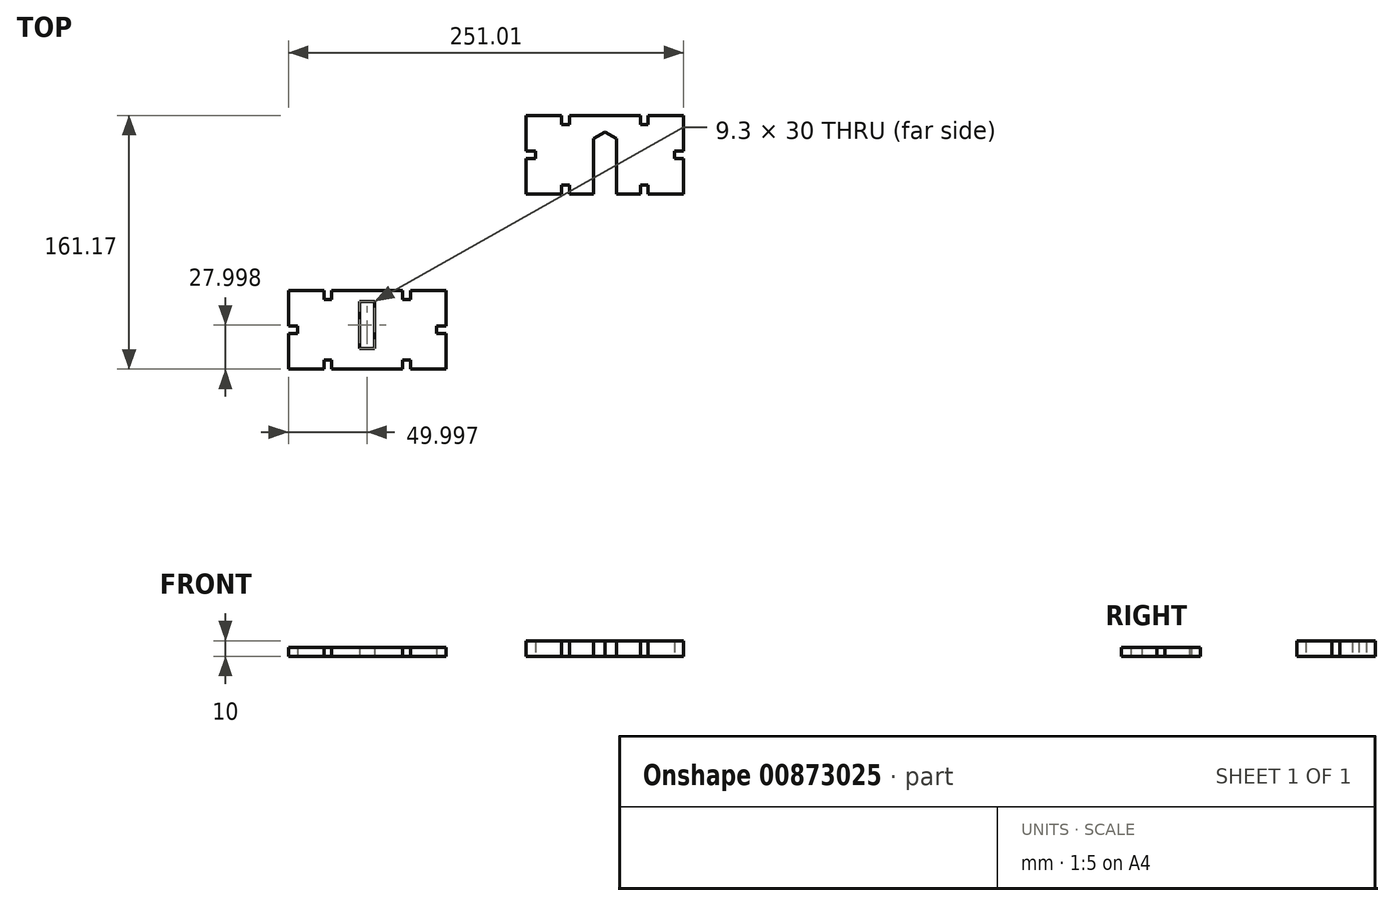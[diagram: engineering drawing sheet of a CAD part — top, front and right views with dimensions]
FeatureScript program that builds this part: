
annotation { "Feature Type Name" : "Feature", "Feature Type Description" : "" }
export const myFeature = defineFeature(function(context is Context, id is Id, definition is map)
    precondition{}
    {
        {
            assignVariable(context, id + "F0", {"name" : "poly_thick", "anyValue" : 5.8});
        }
        {
            var Q0;
            Q0=qCreatedBy(makeId("Top.planeOp"),FACE);
            var sketch = newSketch(context, id + "F1", { "sketchPlane" : qUnion([Q0])});
            skLineSegment(sketch, "E0.bottom", {"start": v(0, 0) * mm, "end": v(22.5, 0) * mm});
            skLineSegment(sketch, "E0.top", {"start": v(0, 50) * mm, "end": v(22.5, 50) * mm});
            skLineSegment(sketch, "E0.left", {"start": v(0, 0) * mm, "end": v(0, 22.5) * mm});
            skLineSegment(sketch, "E0.right", {"start": v(100, 0) * mm, "end": v(100, 22.5) * mm});
            skLineSegment(sketch, "E1.left", {"start": v(42.75, 0) * mm, "end": v(42.75, 35.4) * mm});
            skLineSegment(sketch, "E1.right", {"start": v(57.25, 0) * mm, "end": v(57.25, 35.4) * mm});
            skLineSegment(sketch, "E2", {"start": v(57.25, 35.4) * mm, "end": v(100, 35.4) * mm, "construction": true});
            skLineSegment(sketch, "E3", {"start": v(42.75, 35.4) * mm, "end": v(0, 35.4) * mm, "construction": true});
            skLineSegment(sketch, "E4", {"start": v(50, 0) * mm, "end": v(50, 50) * mm, "construction": true});
            skLineSegment(sketch, "E5", {"start": v(42.75, 35.4) * mm, "end": v(50, 39.58) * mm});
            skLineSegment(sketch, "E6", {"start": v(50, 39.58) * mm, "end": v(57.25, 35.4) * mm});
            skLineSegment(sketch, "E7.trimOffspring", {"start": v(57.25, 0) * mm, "end": v(72.5, 0) * mm});
            skLineSegment(sketch, "E8.bottom", {"start": v(100, 22.5) * mm, "end": v(94.2, 22.5) * mm});
            skLineSegment(sketch, "E8.top", {"start": v(100, 27.5) * mm, "end": v(94.2, 27.5) * mm});
            skLineSegment(sketch, "E8.right", {"start": v(94.2, 22.5) * mm, "end": v(94.2, 27.5) * mm});
            skLineSegment(sketch, "E9", {"start": v(94.2, 22.5) * mm, "end": v(94.2, 0) * mm, "construction": true});
            skLineSegment(sketch, "E10", {"start": v(94.2, 27.5) * mm, "end": v(94.2, 50) * mm, "construction": true});
            skLineSegment(sketch, "E11.MirrorCS", {"start": v(0, 22.5) * mm, "end": v(5.8, 22.5) * mm});
            skLineSegment(sketch, "E12.MirrorCS", {"start": v(5.8, 22.5) * mm, "end": v(5.8, 27.5) * mm});
            skLineSegment(sketch, "E13.MirrorCS", {"start": v(0, 27.5) * mm, "end": v(5.8, 27.5) * mm});
            skLineSegment(sketch, "E14.trimOffspring", {"start": v(0, 27.5) * mm, "end": v(0, 50) * mm});
            skLineSegment(sketch, "E15.trimOffspring", {"start": v(100, 27.5) * mm, "end": v(100, 50) * mm});
            skLineSegment(sketch, "E16", {"start": v(100, 0) * mm, "end": v(50, 50) * mm, "construction": true});
            skLineSegment(sketch, "E17.MirrorCS", {"start": v(0, 0) * mm, "end": v(50, 50) * mm, "construction": true});
            skLineSegment(sketch, "E18.MirrorCS", {"start": v(77.5, 0) * mm, "end": v(77.5, 5.8) * mm});
            skLineSegment(sketch, "E19.MirrorCS", {"start": v(77.5, 5.8) * mm, "end": v(72.5, 5.8) * mm});
            skLineSegment(sketch, "E20.MirrorCS", {"start": v(72.5, 0) * mm, "end": v(72.5, 5.8) * mm});
            skLineSegment(sketch, "E21.MirrorCS", {"start": v(22.5, 0) * mm, "end": v(22.5, 5.8) * mm});
            skLineSegment(sketch, "E22.MirrorCS", {"start": v(22.5, 5.8) * mm, "end": v(27.5, 5.8) * mm});
            skLineSegment(sketch, "E23.MirrorCS", {"start": v(27.5, 0) * mm, "end": v(27.5, 5.8) * mm});
            skLineSegment(sketch, "E24.trimOffspring", {"start": v(27.5, 0) * mm, "end": v(42.75, 0) * mm});
            skLineSegment(sketch, "E25.trimOffspring", {"start": v(77.5, 0) * mm, "end": v(100, 0) * mm});
            skLineSegment(sketch, "E26", {"start": v(100, 50) * mm, "end": v(50, 0) * mm, "construction": true});
            skLineSegment(sketch, "E27", {"start": v(0, 50) * mm, "end": v(50, 0) * mm, "construction": true});
            skLineSegment(sketch, "E28.MirrorCS", {"start": v(72.5, 44.2) * mm, "end": v(77.5, 44.2) * mm});
            skLineSegment(sketch, "E29.MirrorCS", {"start": v(77.5, 50) * mm, "end": v(77.5, 44.2) * mm});
            skLineSegment(sketch, "E30.MirrorCS", {"start": v(72.5, 50) * mm, "end": v(72.5, 44.2) * mm});
            skLineSegment(sketch, "E31.trimOffspring", {"start": v(77.5, 50) * mm, "end": v(100, 50) * mm});
            skLineSegment(sketch, "E32.MirrorCS", {"start": v(22.5, 50) * mm, "end": v(22.5, 44.2) * mm});
            skLineSegment(sketch, "E33.MirrorCS", {"start": v(27.5, 44.2) * mm, "end": v(22.5, 44.2) * mm});
            skLineSegment(sketch, "E34.MirrorCS", {"start": v(27.5, 50) * mm, "end": v(27.5, 44.2) * mm});
            skLineSegment(sketch, "E35.trimOffspring", {"start": v(27.5, 50) * mm, "end": v(72.5, 50) * mm});
            skSolve(sketch);
        }
        {
            var Q0;
            Q0=makeQuery(id+"F1.imprint","IMPRINT",FACE,{"disambiguationData":[TD([[makeQuery(id+"F1.imprint","IMPRINT",EDGE,{"derivedFrom":sQuery(id+"F1.wireOp",EDGE,"E0.bottom")}),1.0]])]});
            extrude(context, id + "F2", {"entities" : qUnion([Q0]), "depth" : 10 * mm, "offsetDistance" : 25 * mm});
        }
        {
            var Q0;
            Q0=qCreatedBy(makeId("Top.planeOp"),FACE);
            var sketch = newSketch(context, id + "F3", { "sketchPlane" : qUnion([Q0])});
            skLineSegment(sketch, "E36.bottom", {"start": v(-151.01, -111.17) * mm, "end": v(-128.51, -111.17) * mm});
            skLineSegment(sketch, "E36.top", {"start": v(-151.01, -61.17) * mm, "end": v(-128.51, -61.17) * mm});
            skLineSegment(sketch, "E36.left", {"start": v(-151.01, -111.17) * mm, "end": v(-151.01, -88.67) * mm});
            skLineSegment(sketch, "E36.right", {"start": v(-51.01, -111.17) * mm, "end": v(-51.01, -88.67) * mm});
            skLineSegment(sketch, "E37", {"start": v(-93.76, -75.78) * mm, "end": v(-51.01, -75.78) * mm, "construction": true});
            skLineSegment(sketch, "E38", {"start": v(-108.26, -75.78) * mm, "end": v(-151.01, -75.78) * mm, "construction": true});
            skLineSegment(sketch, "E39", {"start": v(-101.01, -111.17) * mm, "end": v(-101.01, -61.17) * mm, "construction": true});
            skLineSegment(sketch, "E40.trimOffspring", {"start": v(-88.57, -111.17) * mm, "end": v(-78.51, -111.17) * mm});
            skLineSegment(sketch, "E41.bottom", {"start": v(-51.01, -88.67) * mm, "end": v(-56.81, -88.67) * mm});
            skLineSegment(sketch, "E41.top", {"start": v(-51.01, -83.67) * mm, "end": v(-56.81, -83.67) * mm});
            skLineSegment(sketch, "E41.right", {"start": v(-56.81, -88.67) * mm, "end": v(-56.81, -83.67) * mm});
            skLineSegment(sketch, "E42", {"start": v(-56.81, -88.67) * mm, "end": v(-56.81, -111.17) * mm, "construction": true});
            skLineSegment(sketch, "E43", {"start": v(-56.81, -83.67) * mm, "end": v(-56.81, -61.17) * mm, "construction": true});
            skLineSegment(sketch, "E44.MirrorCS", {"start": v(-151.01, -88.67) * mm, "end": v(-145.21, -88.67) * mm});
            skLineSegment(sketch, "E45.MirrorCS", {"start": v(-145.21, -88.67) * mm, "end": v(-145.21, -83.67) * mm});
            skLineSegment(sketch, "E46.MirrorCS", {"start": v(-151.01, -83.67) * mm, "end": v(-145.21, -83.67) * mm});
            skLineSegment(sketch, "E47.trimOffspring", {"start": v(-151.01, -83.67) * mm, "end": v(-151.01, -61.17) * mm});
            skLineSegment(sketch, "E48.trimOffspring", {"start": v(-51.01, -83.67) * mm, "end": v(-51.01, -61.17) * mm});
            skLineSegment(sketch, "E49", {"start": v(-51.01, -111.17) * mm, "end": v(-101.01, -61.17) * mm, "construction": true});
            skLineSegment(sketch, "E50.MirrorCS", {"start": v(-151.01, -111.17) * mm, "end": v(-101.01, -61.17) * mm, "construction": true});
            skLineSegment(sketch, "E51.MirrorCS", {"start": v(-73.51, -111.17) * mm, "end": v(-73.51, -105.37) * mm});
            skLineSegment(sketch, "E52.MirrorCS", {"start": v(-73.51, -105.37) * mm, "end": v(-78.51, -105.37) * mm});
            skLineSegment(sketch, "E53.MirrorCS", {"start": v(-78.51, -111.17) * mm, "end": v(-78.51, -105.37) * mm});
            skLineSegment(sketch, "E54.MirrorCS", {"start": v(-128.51, -111.17) * mm, "end": v(-128.51, -105.37) * mm});
            skLineSegment(sketch, "E55.MirrorCS", {"start": v(-128.51, -105.37) * mm, "end": v(-123.51, -105.37) * mm});
            skLineSegment(sketch, "E56.MirrorCS", {"start": v(-123.51, -111.17) * mm, "end": v(-123.51, -105.37) * mm});
            skLineSegment(sketch, "E57.trimOffspring", {"start": v(-123.51, -111.17) * mm, "end": v(-113.46, -111.17) * mm});
            skLineSegment(sketch, "E58.trimOffspring", {"start": v(-73.51, -111.17) * mm, "end": v(-51.01, -111.17) * mm});
            skLineSegment(sketch, "E59", {"start": v(-51.01, -61.17) * mm, "end": v(-101.01, -111.17) * mm, "construction": true});
            skLineSegment(sketch, "E60", {"start": v(-151.01, -61.17) * mm, "end": v(-101.01, -111.17) * mm, "construction": true});
            skLineSegment(sketch, "E61.MirrorCS", {"start": v(-78.51, -66.97) * mm, "end": v(-73.51, -66.97) * mm});
            skLineSegment(sketch, "E62.MirrorCS", {"start": v(-73.51, -61.17) * mm, "end": v(-73.51, -66.97) * mm});
            skLineSegment(sketch, "E63.MirrorCS", {"start": v(-78.51, -61.17) * mm, "end": v(-78.51, -66.97) * mm});
            skLineSegment(sketch, "E64.trimOffspring", {"start": v(-73.51, -61.17) * mm, "end": v(-51.01, -61.17) * mm});
            skLineSegment(sketch, "E65.MirrorCS", {"start": v(-128.51, -61.17) * mm, "end": v(-128.51, -66.97) * mm});
            skLineSegment(sketch, "E66.MirrorCS", {"start": v(-123.51, -66.97) * mm, "end": v(-128.51, -66.97) * mm});
            skLineSegment(sketch, "E67.MirrorCS", {"start": v(-123.51, -61.17) * mm, "end": v(-123.51, -66.97) * mm});
            skLineSegment(sketch, "E68.trimOffspring", {"start": v(-123.51, -61.17) * mm, "end": v(-78.51, -61.17) * mm});
            skLineSegment(sketch, "E69", {"start": v(-113.46, -111.17) * mm, "end": v(-88.57, -111.17) * mm});
            skLineSegment(sketch, "E70.bottom", {"start": v(-96.36, -98.17) * mm, "end": v(-105.66, -98.17) * mm});
            skLineSegment(sketch, "E70.top", {"start": v(-96.36, -68.17) * mm, "end": v(-105.66, -68.17) * mm});
            skLineSegment(sketch, "E70.left", {"start": v(-96.36, -98.17) * mm, "end": v(-96.36, -68.17) * mm});
            skLineSegment(sketch, "E70.right", {"start": v(-105.66, -98.17) * mm, "end": v(-105.66, -68.17) * mm});
            skLineSegment(sketch, "E71", {"start": v(-105.66, -83.17) * mm, "end": v(-151.01, -83.17) * mm, "construction": true});
            skLineSegment(sketch, "E72", {"start": v(-96.36, -83.17) * mm, "end": v(-51.01, -83.17) * mm, "construction": true});
            skSolve(sketch);
        }
        {
            var Q0;
            Q0=makeQuery(id+"F3.imprint","IMPRINT",FACE,{"disambiguationData":[TD([[makeQuery(id+"F3.imprint","IMPRINT",EDGE,{"derivedFrom":sQuery(id+"F3.wireOp",EDGE,"E36.bottom")}),1.0]])]});
            extrude(context, id + "F4", {"entities" : qUnion([Q0]), "depth" : (getVariable(context, 'poly_thick')) * mm, "offsetDistance" : 25 * mm});
        }
    });
